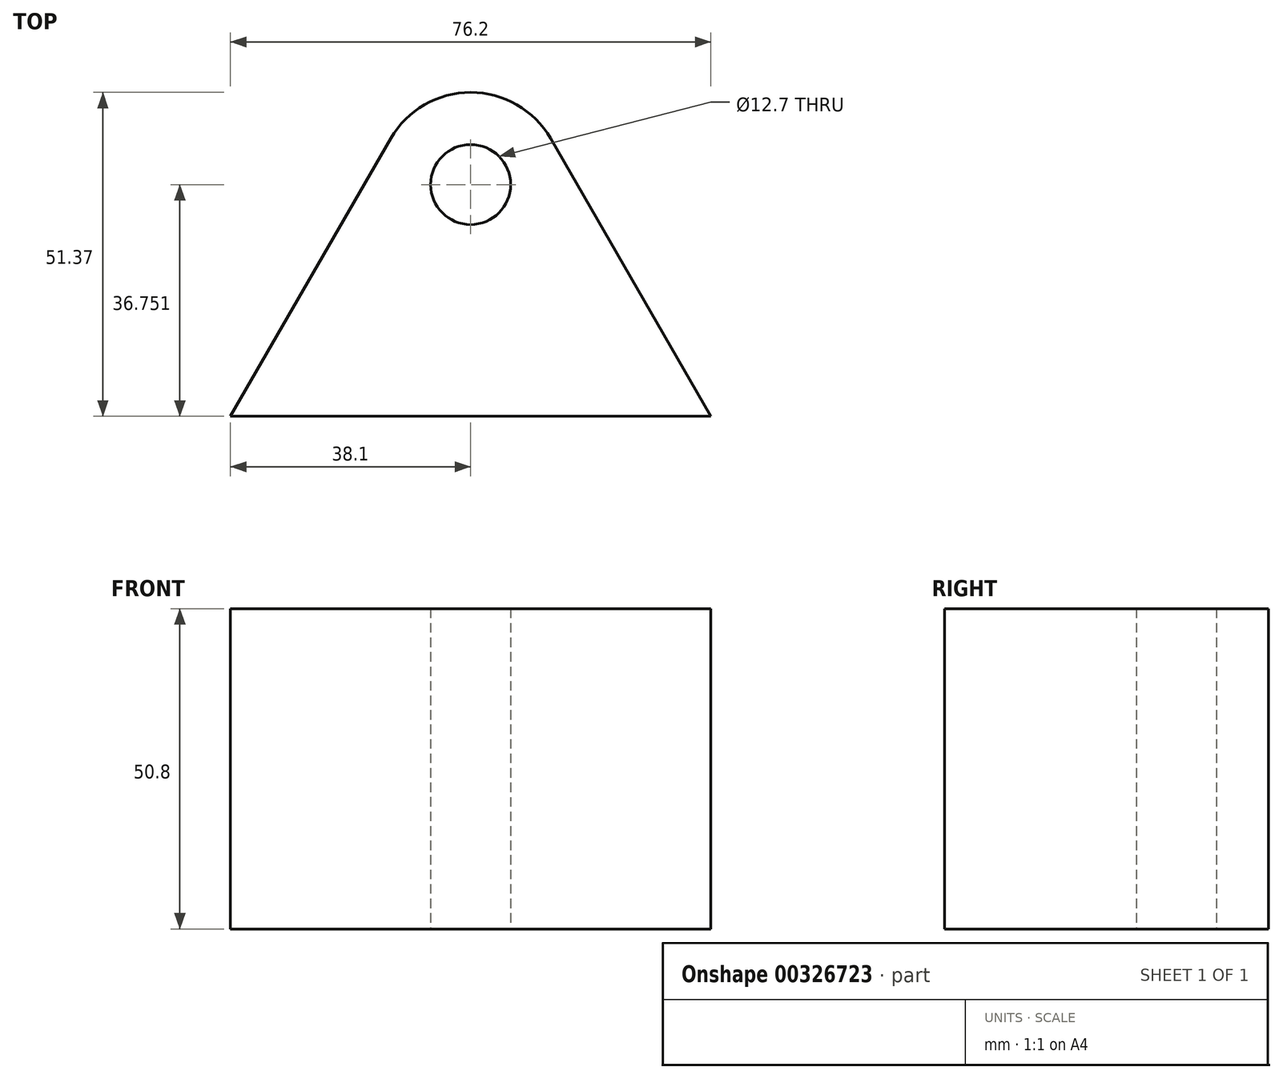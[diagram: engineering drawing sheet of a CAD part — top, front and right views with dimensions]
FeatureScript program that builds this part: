
annotation { "Feature Type Name" : "Feature", "Feature Type Description" : "" }
export const myFeature = defineFeature(function(context is Context, id is Id, definition is map)
    precondition{}
    {
        {
            var Q0;
            Q0=qCreatedBy(makeId("Top.planeOp"),FACE);
            var sketch = newSketch(context, id + "F0", { "sketchPlane" : qUnion([Q0])});
            skLineSegment(sketch, "E0", {"start": v(-38.1, 0) * mm, "end": v(-12.66, 44.06) * mm});
            skLineSegment(sketch, "E1", {"start": v(38.1, 0) * mm, "end": v(12.66, 44.06) * mm});
            skPoint(sketch, "E2.visualSharp", {"position": v(0, 66) * mm});
            skArc(sketch, "E3", {"start": v(12.66, 44.06) * mm, "mid": v(0, 51.37) * mm, "end": v(-12.66, 44.06) * mm});
            skCircle(sketch, "E4", {"center": v(0, 36.75) * mm, "radius": 6.35 * mm});
            skLineSegment(sketch, "E5", {"start": v(-38.1, 0) * mm, "end": v(38.1, 0) * mm});
            skSolve(sketch);
        }
        {
            var Q0;
            Q0=makeQuery(id+"F0.imprint","IMPRINT",FACE,{"disambiguationData":[TD([[makeQuery(id+"F0.imprint","IMPRINT",EDGE,{"derivedFrom":sQuery(id+"F0.wireOp",EDGE,"E0")}),-1.0]])]});
            extrude(context, id + "F1", {"entities" : qUnion([Q0]), "endBound" : BoundingType.SYMMETRIC, "depth" : 50.8 * mm});
        }
    });
